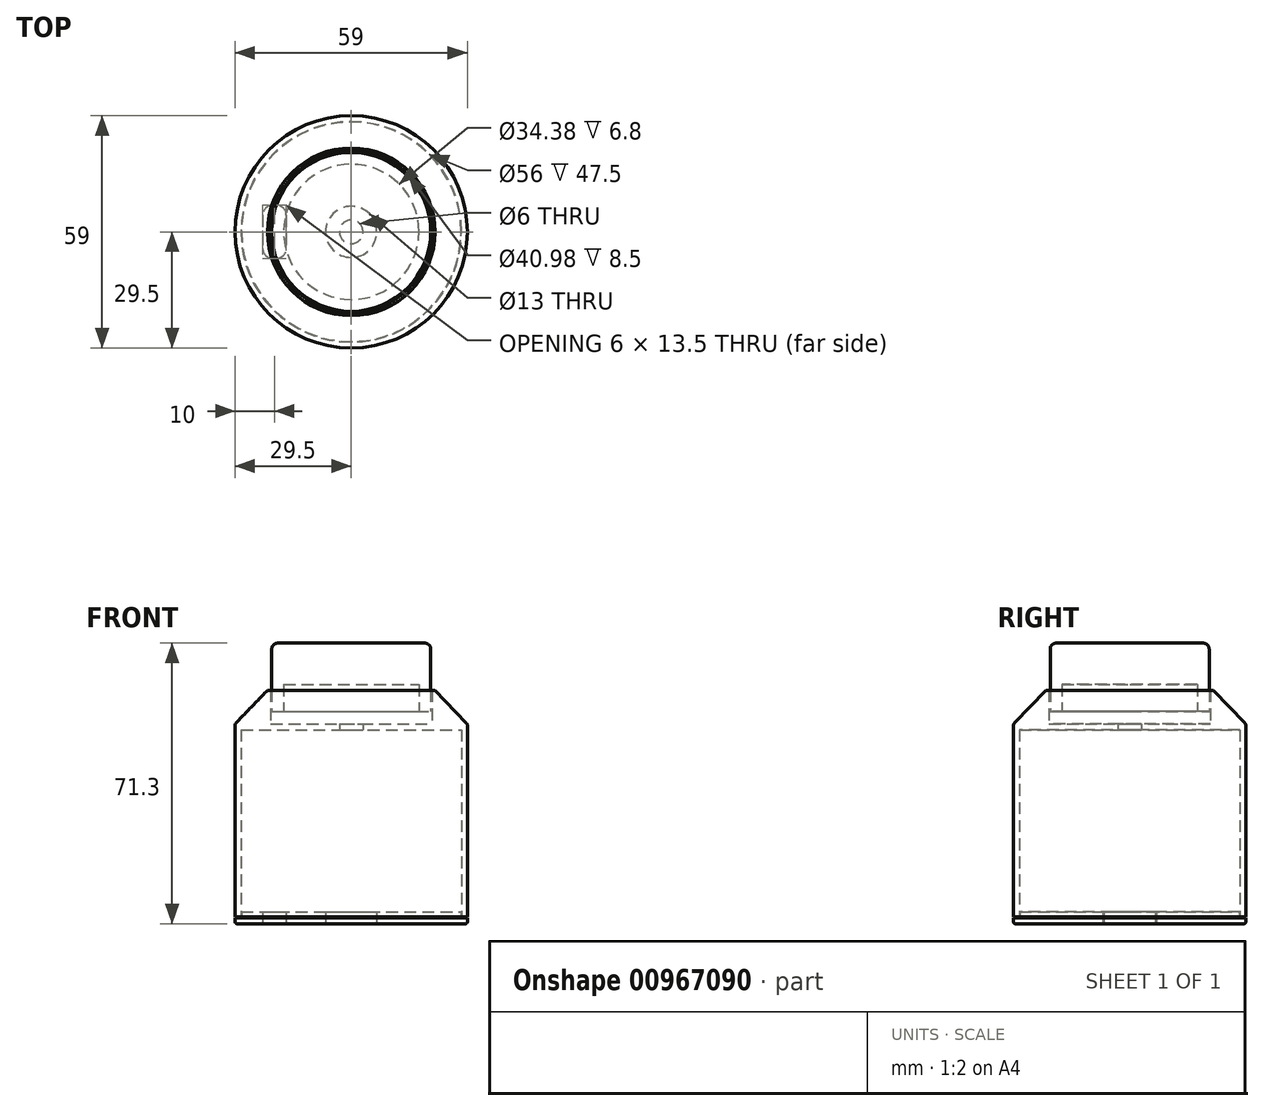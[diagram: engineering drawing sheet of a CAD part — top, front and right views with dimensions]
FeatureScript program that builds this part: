
annotation { "Feature Type Name" : "Feature", "Feature Type Description" : "" }
export const myFeature = defineFeature(function(context is Context, id is Id, definition is map)
    precondition{}
    {
        {
            var Q0;
            Q0=qCreatedBy(makeId("Top.planeOp"),FACE);
            var sketch = newSketch(context, id + "F0", { "sketchPlane" : qUnion([Q0])});
            skCircle(sketch, "E0", {"center": v(0, 0) * mm, "radius": 29.5 * mm});
            skSolve(sketch);
        }
        {
            var Q0;
            Q0=qCreatedBy(makeId("Front.planeOp"),FACE);
            var sketch = newSketch(context, id + "F1", { "sketchPlane" : qUnion([Q0])});
            skLineSegment(sketch, "E1", {"start": v(-29.5, 0) * mm, "end": v(-29.5, 49) * mm});
            skLineSegment(sketch, "E2.1", {"start": v(-29.5, 0) * mm, "end": v(29.5, 0) * mm, "construction": true});
            skLineSegment(sketch, "E3", {"start": v(-29.5, 49) * mm, "end": v(-21.3, 57.5) * mm});
            skLineSegment(sketch, "E4", {"start": v(-21.3, 57.5) * mm, "end": v(-20.5, 57.5) * mm});
            skLineSegment(sketch, "E5", {"start": v(-20.5, 57.5) * mm, "end": v(-20.5, 47.5) * mm, "construction": true});
            skLineSegment(sketch, "E6", {"start": v(-20.5, 47.5) * mm, "end": v(-28, 47.5) * mm});
            skLineSegment(sketch, "E7", {"start": v(-28, 47.5) * mm, "end": v(-28, 0) * mm});
            skLineSegment(sketch, "E8", {"start": v(-28, 0) * mm, "end": v(-29.5, 0) * mm});
            skLineSegment(sketch, "E9", {"start": v(-20.5, 57.5) * mm, "end": v(-20.5, 49) * mm});
            skLineSegment(sketch, "E10", {"start": v(-20.5, 49) * mm, "end": v(-3, 49) * mm});
            skLineSegment(sketch, "E11", {"start": v(-3, 49) * mm, "end": v(-3, 47.5) * mm});
            skLineSegment(sketch, "E12", {"start": v(-3, 47.5) * mm, "end": v(-20.5, 47.5) * mm});
            skLineSegment(sketch, "E13", {"start": v(0, 0) * mm, "end": v(0, 67.8) * mm, "construction": true});
            skSolve(sketch);
        }
        {
            var Q0;
            Q0=qSketchRegion(id+"F1",true);
            var Q1;
            Q1=sQuery(id+"F1.wireOp",EDGE,"E13");
            revolve(context, id + "F2", {"surfaceOperationType" : NewSurfaceOperationType.NEW, "entities" : qUnion([Q0]), "axis" : qUnion([Q1]), "revolveType" : RevolveType.FULL});
        }
        {
            var Q0;
            Q0=qCreatedBy(makeId("Front.planeOp"),FACE);
            var sketch = newSketch(context, id + "F3", { "sketchPlane" : qUnion([Q0])});
            skLineSegment(sketch, "E14", {"start": v(-20.2, 52.2) * mm, "end": v(-20.2, 69.5) * mm});
            skLineSegment(sketch, "E15", {"start": v(-20.2, 69.5) * mm, "end": v(0, 69.5) * mm});
            skLineSegment(sketch, "E16", {"start": v(0, 69.5) * mm, "end": v(0, 59) * mm});
            skLineSegment(sketch, "E17", {"start": v(0, 59) * mm, "end": v(-17.2, 59) * mm});
            skLineSegment(sketch, "E18", {"start": v(-17.2, 59) * mm, "end": v(-17.2, 52.2) * mm});
            skLineSegment(sketch, "E19", {"start": v(-17.2, 52.2) * mm, "end": v(-20.2, 52.2) * mm});
            skSolve(sketch);
        }
        {
            var Q0;
            Q0=makeQuery(id+"F3.imprint","IMPRINT",FACE,{"disambiguationData":[TD([[makeQuery(id+"F3.imprint","IMPRINT",EDGE,{"derivedFrom":sQuery(id+"F3.wireOp",EDGE,"E14")}),-1.0]])]});
            var Q1;
            Q1=sQuery(id+"F1.wireOp",EDGE,"E13");
            revolve(context, id + "F4", {"surfaceOperationType" : NewSurfaceOperationType.NEW, "entities" : qUnion([Q0]), "axis" : qUnion([Q1]), "revolveType" : RevolveType.FULL});
        }
        {
            var Q0;
            Q0=makeQuery(id+"F4.opRevolve","SWEPT_EDGE",EDGE,{"disambiguationData":[OSD([sQuery(id+"F3.wireOp",EDGE,"E14"),sQuery(id+"F3.wireOp",EDGE,"E15")])]});
            fillet(context, id + "F5", {"entities" : qUnion([Q0]), "radius" : 1.5 * mm, "tangentPropagation" : true, "allowEdgeOverflow" : false});
        }
        {
            var Q0;
            Q0=makeQuery(id+"F2.opRevolve","SWEPT_EDGE",EDGE,{"disambiguationData":[OSD([sQuery(id+"F1.wireOp",EDGE,"E1"),sQuery(id+"F1.wireOp",EDGE,"E3")])]});
            fillet(context, id + "F6", {"entities" : qUnion([Q0]), "radius" : 1 * mm, "tangentPropagation" : true, "allowEdgeOverflow" : false});
        }
        {
            var Q0;
            Q0=qCreatedBy(makeId("Front.planeOp"),FACE);
            var sketch = newSketch(context, id + "F7", { "sketchPlane" : qUnion([Q0])});
            skLineSegment(sketch, "E20", {"start": v(0, -1.8) * mm, "end": v(-29.5, -1.8) * mm, "construction": true});
            skLineSegment(sketch, "E21", {"start": v(-29.5, -1.8) * mm, "end": v(-29.5, -0.3) * mm});
            skLineSegment(sketch, "E22", {"start": v(-29.5, -0.3) * mm, "end": v(-27.9, -0.3) * mm});
            skLineSegment(sketch, "E23", {"start": v(-27.9, -0.3) * mm, "end": v(-27.9, 1.2) * mm});
            skLineSegment(sketch, "E24", {"start": v(-27.9, 1.2) * mm, "end": v(0, 1.2) * mm, "construction": true});
            skLineSegment(sketch, "E25", {"start": v(0, 1.2) * mm, "end": v(0, -1.8) * mm, "construction": true});
            skLineSegment(sketch, "E26", {"start": v(-29.5, -1.8) * mm, "end": v(-6.5, -1.8) * mm});
            skLineSegment(sketch, "E27", {"start": v(-6.5, -1.8) * mm, "end": v(-6.5, 1.2) * mm});
            skLineSegment(sketch, "E28", {"start": v(-6.5, 1.2) * mm, "end": v(-27.9, 1.2) * mm});
            skSolve(sketch);
        }
        {
            var Q0;
            Q0=makeQuery(id+"F7.imprint","IMPRINT",FACE,{"disambiguationData":[TD([[makeQuery(id+"F7.imprint","IMPRINT",EDGE,{"derivedFrom":sQuery(id+"F7.wireOp",EDGE,"E21")}),-1.0]])]});
            var Q1;
            Q1=sQuery(id+"F1.wireOp",EDGE,"E13");
            revolve(context, id + "F8", {"surfaceOperationType" : NewSurfaceOperationType.NEW, "entities" : qUnion([Q0]), "axis" : qUnion([Q1]), "revolveType" : RevolveType.FULL});
        }
        {
            var Q0;
            Q0=makeQuery(id+"F8.opRevolve","SWEPT_FACE",FACE,{"disambiguationData":[OSD([sQuery(id+"F7.wireOp",EDGE,"E26")])]});
            var sketch = newSketch(context, id + "F9", { "sketchPlane" : qUnion([Q0])});
            skLineSegment(sketch, "E29.bottom", {"start": v(-20, -6.75) * mm, "end": v(-19, -6.75) * mm});
            skLineSegment(sketch, "E29.top", {"start": v(-20, 6.75) * mm, "end": v(-19, 6.75) * mm});
            skLineSegment(sketch, "E29.left", {"start": v(-22.5, -4.25) * mm, "end": v(-22.5, 4.25) * mm});
            skLineSegment(sketch, "E29.right", {"start": v(-16.5, -4.25) * mm, "end": v(-16.5, 4.25) * mm});
            skPoint(sketch, "E29.middle", {"position": v(-19.5, 0) * mm});
            skPoint(sketch, "E30.visualSharp", {"position": v(-16.5, -6.75) * mm});
            skArc(sketch, "E30.filletArc", {"start": v(-19, -6.75) * mm, "mid": v(-17.23, -6.02) * mm, "end": v(-16.5, -4.25) * mm});
            skPoint(sketch, "E31.visualSharp", {"position": v(-22.5, -6.75) * mm});
            skArc(sketch, "E31.filletArc", {"start": v(-22.5, -4.25) * mm, "mid": v(-21.77, -6.02) * mm, "end": v(-20, -6.75) * mm});
            skPoint(sketch, "E32.visualSharp", {"position": v(-22.5, 6.75) * mm});
            skArc(sketch, "E32.filletArc", {"start": v(-20, 6.75) * mm, "mid": v(-21.77, 6.02) * mm, "end": v(-22.5, 4.25) * mm});
            skPoint(sketch, "E33.visualSharp", {"position": v(-16.5, 6.75) * mm});
            skArc(sketch, "E33.filletArc", {"start": v(-16.5, 4.25) * mm, "mid": v(-17.23, 6.02) * mm, "end": v(-19, 6.75) * mm});
            skSolve(sketch);
        }
        {
            var Q0;
            Q0=qSketchRegion(id+"F9",true);
            extrude(context, id + "F10", {"entities" : qUnion([Q0]), "operationType" : NewBodyOperationType.REMOVE, "oppositeDirection" : true, "depth" : 25 * mm, "offsetDistance" : 25 * mm});
        }
        {
            var Q0;
            Q0=makeQuery(id+"F8.opRevolve","SWEPT_EDGE",EDGE,{"disambiguationData":[OSD([sQuery(id+"F7.wireOp",EDGE,"E21"),sQuery(id+"F7.wireOp",EDGE,"E26")])]});
            fillet(context, id + "F11", {"entities" : qUnion([Q0]), "radius" : 0.5 * mm, "tangentPropagation" : true, "allowEdgeOverflow" : false});
        }
    });
